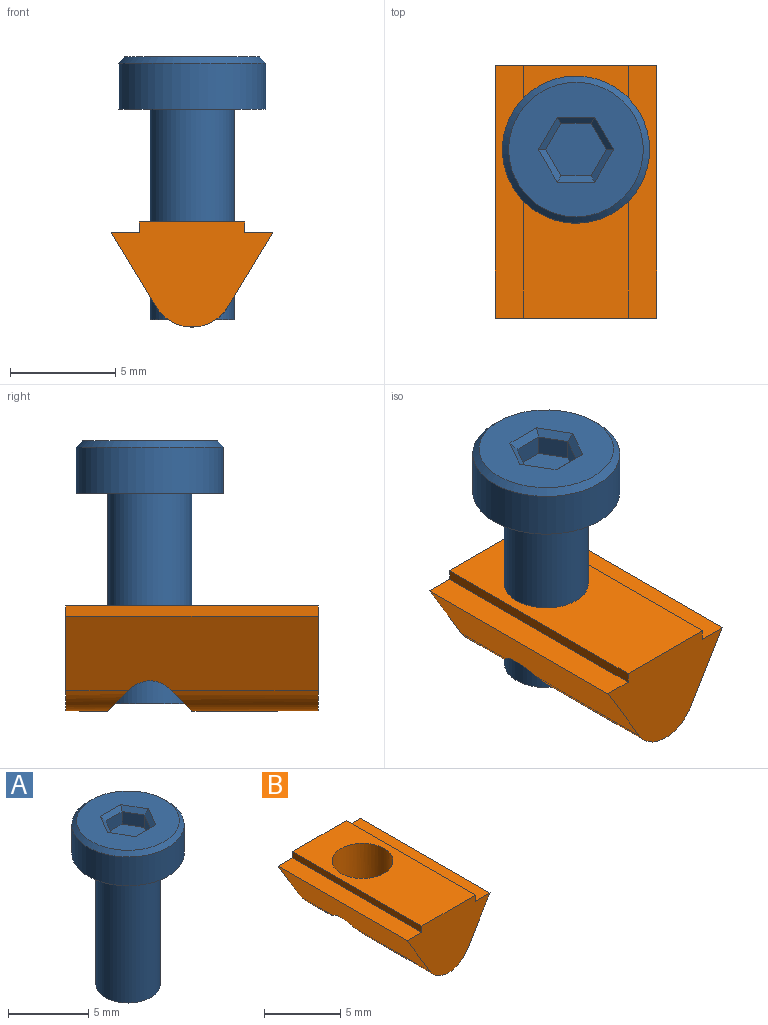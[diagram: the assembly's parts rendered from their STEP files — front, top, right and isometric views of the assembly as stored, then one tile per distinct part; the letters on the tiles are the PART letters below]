
ASSEMBLY  parts=2 mates=1
PART A: 19 faces, bbox 7x7x12.5 mm
  f0: cylinder r=3.5mm len=7mm, axis (0,0,1), area 48.4mm2, adj f1,f18
  f1: plane 7x7mm, normal (0,0,-1), area 25.9mm2, adj f0,f3
  f2: plane 6.4x6.4mm, normal (0,0,1), area 23.8mm2, adj f12,f13,f14,f15,f16,f17,f18
  f3: cylinder r=2mm len=10mm, axis (0,0,1), area 125.7mm2, adj f1,f4
  f4: plane 4x4mm, normal (0,0,-1), area 12.6mm2, adj f3
  f5: plane 1.44x0.95mm, normal (0,-1,0), area 1.4mm2, adj f6,f10,f11,f16
  f6: plane 1.25x0.95mm, normal (0.87,-0.5,0), area 1.4mm2, adj f5,f7,f11,f17
  f7: plane 1.25x0.95mm, normal (0.87,0.5,0), area 1.4mm2, adj f6,f8,f11,f15
  f8: plane 1.44x0.95mm, normal (0,1,0), area 1.4mm2, adj f7,f9,f11,f13
  f9: plane 1.25x0.95mm, normal (-0.87,0.5,0), area 1.4mm2, adj f8,f10,f11,f12
  f10: plane 1.25x0.95mm, normal (-0.87,-0.5,0), area 1.4mm2, adj f5,f9,f11,f14
  f11: plane 2.89x2.5mm, normal (0,0,1), area 5.4mm2, adj f5,f6,f7,f8,f9,f10
  f12: plane 1.55x1.07mm, normal (-0.61,0.35,0.71), area 0.7mm2, adj f2,f9,f13,f14
  f13: plane 1.79x0.3mm, normal (0,0.71,0.71), area 0.7mm2, adj f2,f8,f12,f15
  f14: plane 1.55x1.07mm, normal (-0.61,-0.35,0.71), area 0.7mm2, adj f2,f10,f12,f16
  f15: plane 1.55x1.07mm, normal (0.61,0.35,0.71), area 0.7mm2, adj f2,f7,f13,f17
  f16: plane 1.79x0.3mm, normal (0,-0.71,0.71), area 0.7mm2, adj f2,f5,f14,f17
  f17: plane 1.55x1.07mm, normal (0.61,-0.35,0.71), area 0.7mm2, adj f2,f6,f15,f16
  f18: cone r=3.5mm half-angle=45deg, axis (0,0,-1), area 8.9mm2, adj f0,f2
PART B: 12 faces, bbox 7.7x12x5 mm
  f0: cylinder r=2mm len=3.42mm, axis (0,1,0), area 9.6mm2, adj f2,f4,f10,f11
  f1: plane 12x1.35mm, normal (0,0,1), area 16.2mm2, adj f2,f8,f9,f10
  f2: plane 12x3.54mm, normal (-0.86,0,-0.52), area 48.8mm2, adj f0,f1,f3,f9,f10,f11
  f3: cylinder r=2mm len=6.96mm, axis (0,1,0), area 26mm2, adj f2,f4,f9,f11
  f4: plane 12x3.54mm, normal (0.86,0,-0.52), area 48.8mm2, adj f0,f3,f5,f9,f10,f11
  f5: plane 12x1.35mm, normal (0,0,1), area 16.2mm2, adj f4,f6,f9,f10
  f6: plane 12x0.5mm, normal (1,0,0), area 6mm2, adj f5,f7,f9,f10
  f7: plane 12x5mm, normal (0,0,1), area 47.4mm2, adj f6,f8,f9,f10,f11
  f8: plane 12x0.5mm, normal (-1,0,0), area 6mm2, adj f1,f7,f9,f10
  f9: plane 7.7x5mm, normal (0,-1,0), area 24.5mm2, adj f1,f2,f3,f4,f5,f6,f7,f8
  f10: plane 7.7x5mm, normal (0,1,0), area 24.5mm2, adj f0,f1,f2,f4,f5,f6,f7,f8
  f11: cylinder r=2mm len=5mm, axis (0,0,1), area 54.5mm2, adj f0,f2,f3,f4,f7
PLACE A t=(-2.68,-24.66,9.77)mm
PLACE B t=(-2.68,5.47,1.42)mm
MATE fastened B.f11 <-> A.f0  axis (0,0,1) through (-2.68,1.47,1.92)mm
